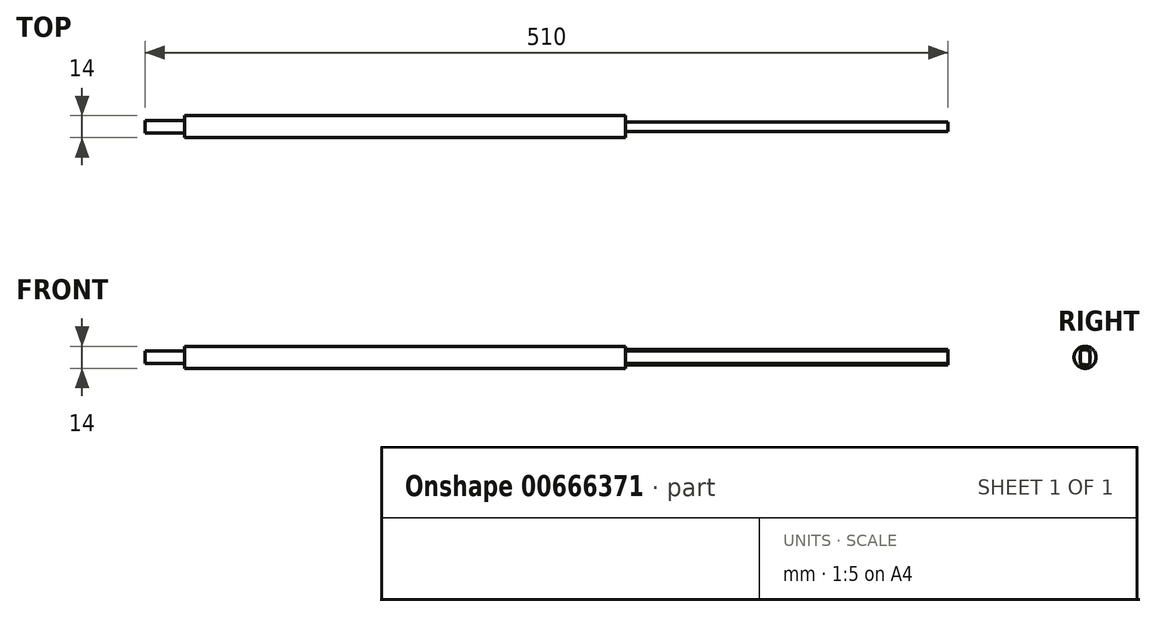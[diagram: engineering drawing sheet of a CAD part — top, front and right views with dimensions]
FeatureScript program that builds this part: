
annotation { "Feature Type Name" : "Feature", "Feature Type Description" : "" }
export const myFeature = defineFeature(function(context is Context, id is Id, definition is map)
    precondition{}
    {
        {
            var Q0;
            Q0=qCreatedBy(makeId("Front.planeOp"),FACE);
            var sketch = newSketch(context, id + "F0", { "sketchPlane" : qUnion([Q0])});
            skLineSegment(sketch, "E0", {"start": v(0, 0) * mm, "end": v(510, 0) * mm});
            skLineSegment(sketch, "E1", {"start": v(510, 0) * mm, "end": v(510, 5) * mm});
            skLineSegment(sketch, "E2", {"start": v(0, 0) * mm, "end": v(0, 4) * mm});
            skLineSegment(sketch, "E3", {"start": v(0, 4) * mm, "end": v(25, 4) * mm});
            skLineSegment(sketch, "E4", {"start": v(25, 4) * mm, "end": v(25, 7) * mm});
            skLineSegment(sketch, "E5", {"start": v(25, 7) * mm, "end": v(305, 7) * mm});
            skLineSegment(sketch, "E6", {"start": v(305, 7) * mm, "end": v(305, 5) * mm});
            skLineSegment(sketch, "E7", {"start": v(305, 5) * mm, "end": v(510, 5) * mm});
            skSolve(sketch);
        }
        {
            var Q0;
            Q0=makeQuery(id+"F0.imprint","IMPRINT",FACE,{"disambiguationData":[TD([[makeQuery(id+"F0.imprint","IMPRINT",EDGE,{"derivedFrom":sQuery(id+"F0.wireOp",EDGE,"E0")}),1.0]])]});
            var Q1;
            Q1=sQuery(id+"F0.wireOp",EDGE,"E0");
            revolve(context, id + "F1", {"entities" : qUnion([Q0]), "axis" : qUnion([Q1]), "revolveType" : RevolveType.FULL});
        }
        {
            var Q0;
            Q0=makeQuery(id+"F1.opRevolve","SWEPT_FACE",FACE,{"disambiguationData":[OSD([sQuery(id+"F0.wireOp",EDGE,"E1")])]});
            var sketch = newSketch(context, id + "F2", { "sketchPlane" : qUnion([Q0])});
            skArc(sketch, "E8", {"start": v(3, -4) * mm, "mid": v(5, 0) * mm, "end": v(3, 4) * mm});
            skLineSegment(sketch, "E9.0", {"start": v(3, -4) * mm, "end": v(3, 4) * mm});
            skLineSegment(sketch, "E10.0", {"start": v(-3, -4) * mm, "end": v(-3, 4) * mm});
            skArc(sketch, "E11.trimOffspring", {"start": v(-3, 4) * mm, "mid": v(-5, 0) * mm, "end": v(-3, -4) * mm});
            skSolve(sketch);
        }
        {
            var Q0;
            Q0=makeQuery(id+"F2.imprint","IMPRINT",FACE,{"disambiguationData":[TD([[makeQuery(id+"F2.imprint","IMPRINT",EDGE,{"derivedFrom":sQuery(id+"F2.wireOp",EDGE,"E10.0")}),1.0]])]});
            var Q1;
            Q1=makeQuery(id+"F2.imprint","IMPRINT",FACE,{"disambiguationData":[TD([[makeQuery(id+"F2.imprint","IMPRINT",EDGE,{"derivedFrom":sQuery(id+"F2.wireOp",EDGE,"E8")}),-1.0]])]});
            extrude(context, id + "F3", {"entities" : qUnion([Q0, Q1]), "operationType" : NewBodyOperationType.REMOVE, "oppositeDirection" : true, "depth" : 205 * mm, "offsetDistance" : 25 * mm});
        }
    });
